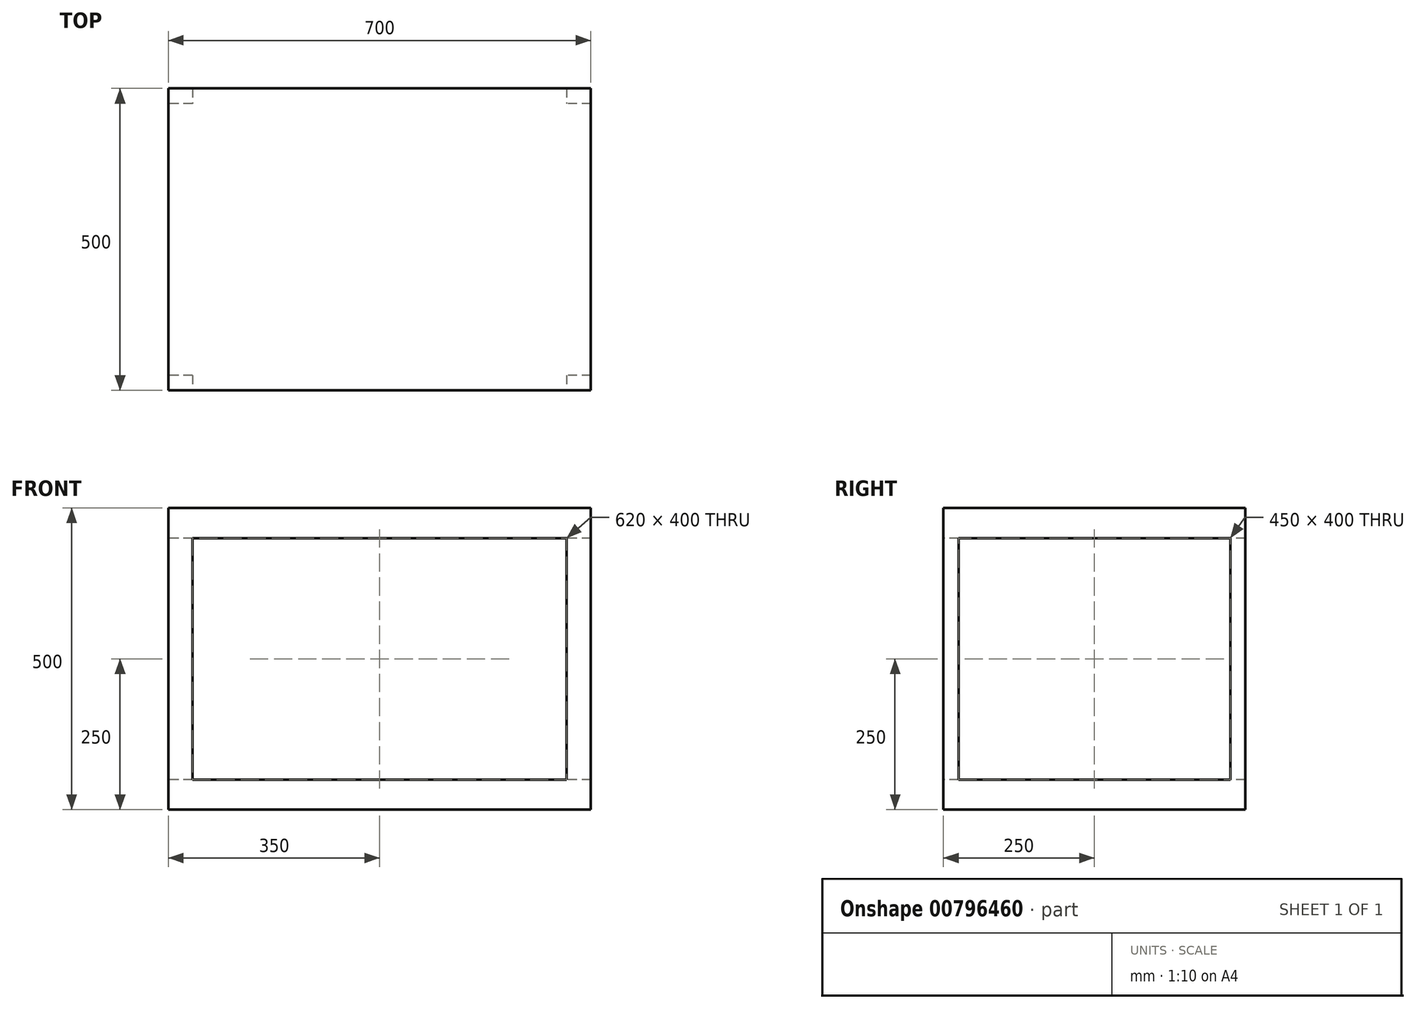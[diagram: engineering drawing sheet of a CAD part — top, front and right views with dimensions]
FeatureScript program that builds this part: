
annotation { "Feature Type Name" : "Feature", "Feature Type Description" : "" }
export const myFeature = defineFeature(function(context is Context, id is Id, definition is map)
    precondition{}
    {
        {
            var Q0;
            Q0=qCreatedBy(makeId("Top.planeOp"),FACE);
            var sketch = newSketch(context, id + "F0", { "sketchPlane" : qUnion([Q0])});
            skLineSegment(sketch, "E0.bottom", {"start": v(-350, 250) * mm, "end": v(350, 250) * mm});
            skLineSegment(sketch, "E0.top", {"start": v(-350, -250) * mm, "end": v(350, -250) * mm});
            skLineSegment(sketch, "E0.left", {"start": v(-350, 250) * mm, "end": v(-350, -250) * mm});
            skLineSegment(sketch, "E0.right", {"start": v(350, 250) * mm, "end": v(350, -250) * mm});
            skSolve(sketch);
        }
        {
            var Q0;
            Q0 = qSketchRegion(id + "F0", true);
            extrude(context, id + "F1", {"entities" : qUnion([Q0]), "depth" : 500 * mm, "offsetDistance" : 25 * mm});
        }
        {
            var Q0;
            Q0=makeQuery(id+"F1.opExtrude","SWEPT_FACE",FACE,{"disambiguationData":[OSD([sQuery(id+"F0.wireOp",EDGE,"E0.top")])]});
            var sketch = newSketch(context, id + "F2", { "sketchPlane" : qUnion([Q0])});
            skLineSegment(sketch, "E1.bottom", {"start": v(-310, 450) * mm, "end": v(310, 450) * mm});
            skLineSegment(sketch, "E1.top", {"start": v(-310, 50) * mm, "end": v(310, 50) * mm});
            skLineSegment(sketch, "E1.left", {"start": v(-310, 450) * mm, "end": v(-310, 50) * mm});
            skLineSegment(sketch, "E1.right", {"start": v(310, 450) * mm, "end": v(310, 50) * mm});
            skSolve(sketch);
        }
        {
            var Q0;
            Q0 = qSketchRegion(id + "F2", true);
            extrude(context, id + "F3", {"entities" : qUnion([Q0]), "operationType" : NewBodyOperationType.REMOVE, "oppositeDirection" : true, "depth" : 810 * mm, "offsetDistance" : 25 * mm});
        }
        {
            var Q0;
            Q0=makeQuery(id+"F1.opExtrude","SWEPT_FACE",FACE,{"disambiguationData":[OSD([sQuery(id+"F0.wireOp",EDGE,"E0.left")])]});
            var sketch = newSketch(context, id + "F4", { "sketchPlane" : qUnion([Q0])});
            skLineSegment(sketch, "E2.bottom", {"start": v(-225, 450) * mm, "end": v(225, 450) * mm});
            skLineSegment(sketch, "E2.top", {"start": v(-225, 50) * mm, "end": v(225, 50) * mm});
            skLineSegment(sketch, "E2.left", {"start": v(-225, 450) * mm, "end": v(-225, 50) * mm});
            skLineSegment(sketch, "E2.right", {"start": v(225, 450) * mm, "end": v(225, 50) * mm});
            skSolve(sketch);
        }
        {
            var Q0;
            Q0 = qSketchRegion(id + "F4", true);
            extrude(context, id + "F5", {"entities" : qUnion([Q0]), "operationType" : NewBodyOperationType.REMOVE, "oppositeDirection" : true, "depth" : 777 * mm, "offsetDistance" : 25 * mm});
        }
    });
